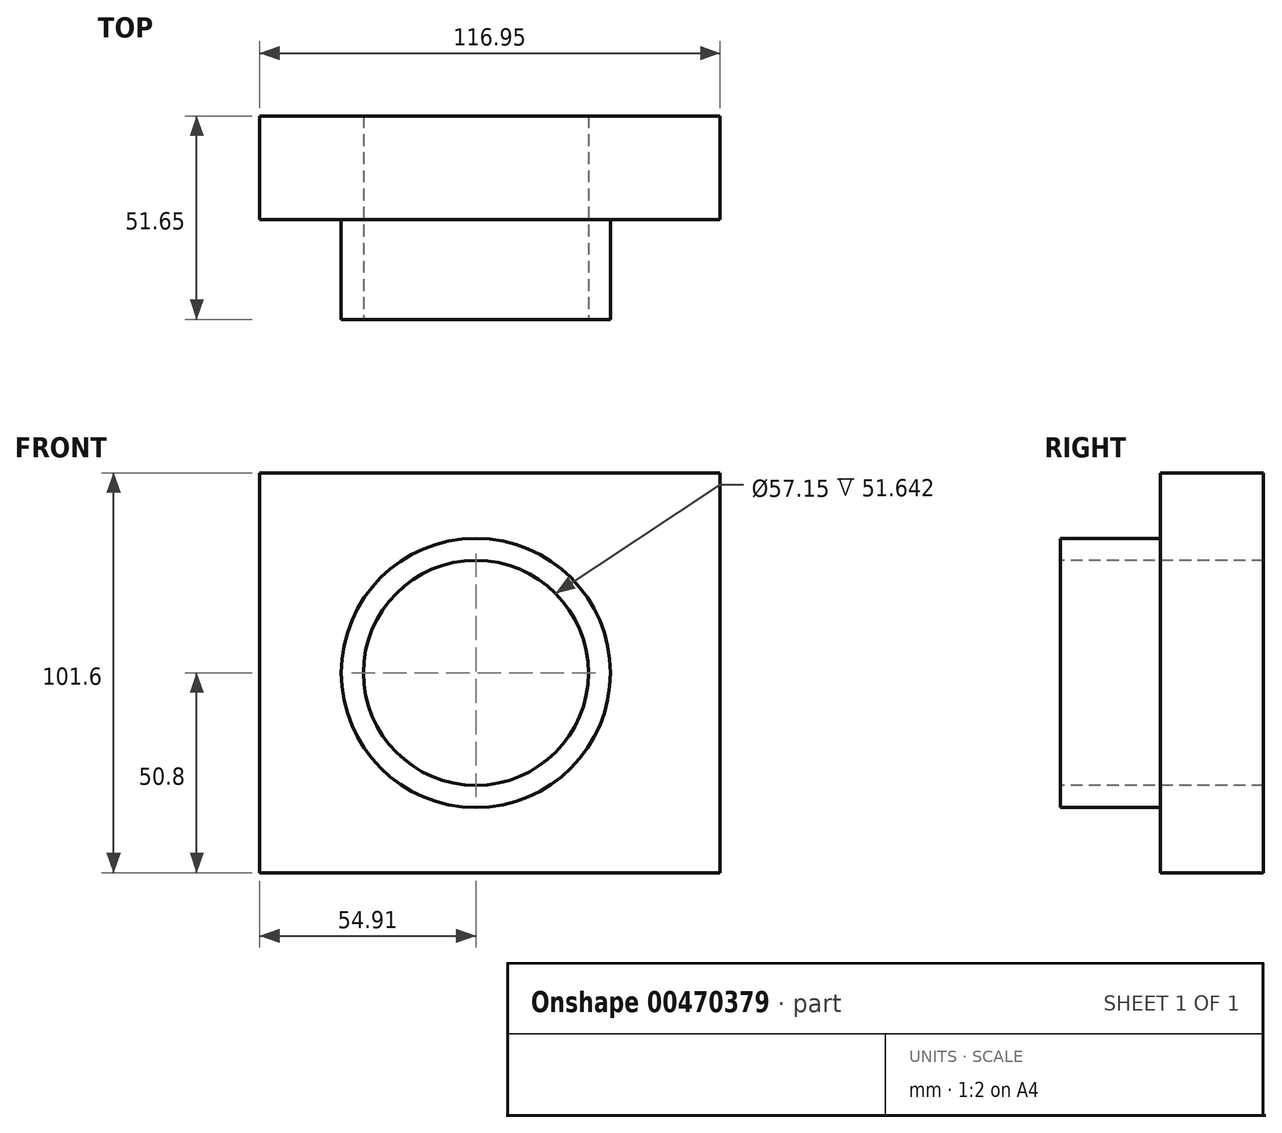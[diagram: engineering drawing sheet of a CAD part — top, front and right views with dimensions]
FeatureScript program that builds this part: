
annotation { "Feature Type Name" : "Feature", "Feature Type Description" : "" }
export const myFeature = defineFeature(function(context is Context, id is Id, definition is map)
    precondition{}
    {
        {
            var Q0;
            Q0=qCreatedBy(makeId("Top.planeOp"),FACE);
            var sketch = newSketch(context, id + "F0", { "sketchPlane" : qUnion([Q0])});
            skLineSegment(sketch, "E0.bottom", {"start": v(-54.9, 46.64) * mm, "end": v(62.04, 46.64) * mm});
            skLineSegment(sketch, "E0.top", {"start": v(-54.9, 20.4) * mm, "end": v(62.04, 20.4) * mm});
            skLineSegment(sketch, "E0.left", {"start": v(-54.9, 46.64) * mm, "end": v(-54.9, 20.4) * mm});
            skLineSegment(sketch, "E0.right", {"start": v(62.04, 46.64) * mm, "end": v(62.04, 20.4) * mm});
            skSolve(sketch);
        }
        {
            var Q0;
            Q0=makeQuery(id+"F0.imprint","IMPRINT",FACE,{"disambiguationData":[TD([[makeQuery(id+"F0.imprint","IMPRINT",EDGE,{"derivedFrom":sQuery(id+"F0.wireOp",EDGE,"E0.bottom")}),-1.0]])]});
            extrude(context, id + "F1", {"entities" : qUnion([Q0]), "depth" : 101.6 * mm});
        }
        {
            var Q0;
            Q0=makeQuery(id+"F1.opExtrude","SWEPT_FACE",FACE,{"disambiguationData":[OSD([sQuery(id+"F0.wireOp",EDGE,"E0.top")])]});
            var sketch = newSketch(context, id + "F2", { "sketchPlane" : qUnion([Q0])});
            skCircle(sketch, "E1", {"center": v(0, 50.8) * mm, "radius": 32.82 * mm});
            skPoint(sketch, "E1.centerSnap0", {"position": v(-54.9, 50.8) * mm});
            skSolve(sketch);
        }
        {
            var Q0;
            Q0=sQuery(id+"F2.wireOp",VERTEX,"E1.center");
            var Q1;
            Q1=makeQuery(id+"F1.opExtrude","SWEPT_BODY",BODY,{"disambiguationData":[OSD([sQuery(id+"F0.wireOp",EDGE,"E0.bottom"),sQuery(id+"F0.wireOp",EDGE,"E0.top"),sQuery(id+"F0.wireOp",EDGE,"E0.left"),sQuery(id+"F0.wireOp",EDGE,"E0.right")])]});
            hole(context, id + "F3", {"style" : HoleStyle.SIMPLE, "endStyle" : HoleEndStyle.THROUGH, "holeDiameter" : 57.15 * mm, "isTappedThrough" : true, "tappedDepth" : 12.7 * mm, "tapClearance" : 3, "locations" : qUnion([Q0]), "scope" : qUnion([Q1])});
        }
        {
            var Q0;
            Q0=makeQuery(id+"F1.opExtrude","SWEPT_FACE",FACE,{"disambiguationData":[OSD([sQuery(id+"F0.wireOp",EDGE,"E0.top")])]});
            var sketch = newSketch(context, id + "F4", { "sketchPlane" : qUnion([Q0])});
            skCircle(sketch, "E2", {"center": v(0, 50.8) * mm, "radius": 34.19 * mm});
            skSolve(sketch);
        }
        {
            var Q0;
            Q0=makeQuery(id+"F4.imprint","IMPRINT",FACE,{"disambiguationData":[TD([[makeQuery(id+"F4.imprint","IMPRINT",EDGE,{"derivedFrom":sQuery(id+"F4.wireOp",EDGE,"E2")}),1.0]])]});
            extrude(context, id + "F5", {"entities" : qUnion([Q0]), "operationType" : NewBodyOperationType.ADD, "depth" : 25.4 * mm});
        }
    });
